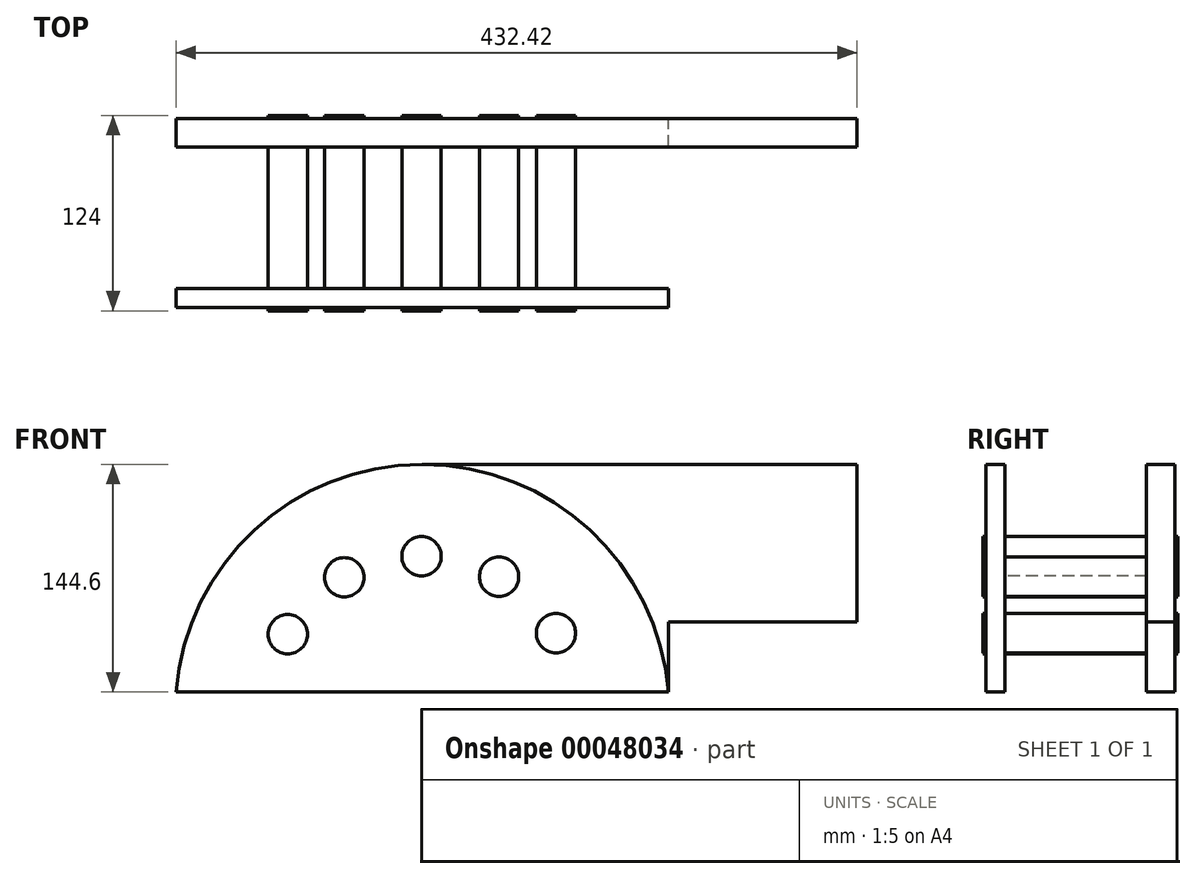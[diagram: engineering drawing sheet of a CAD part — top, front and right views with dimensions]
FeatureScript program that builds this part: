
annotation { "Feature Type Name" : "Feature", "Feature Type Description" : "" }
export const myFeature = defineFeature(function(context is Context, id is Id, definition is map)
    precondition{}
    {
        {
            var Q0;
            Q0=qCreatedBy(makeId("Front.planeOp"),FACE);
            var sketch = newSketch(context, id + "F0", { "sketchPlane" : qUnion([Q0])});
            skLineSegment(sketch, "E0.bottom", {"start": v(-26.1, 0) * mm, "end": v(-302.21, 0) * mm});
            skLineSegment(sketch, "E0.top", {"start": v(-26.1, -100) * mm, "end": v(-145.92, -100) * mm});
            skLineSegment(sketch, "E1", {"start": v(-458.51, -144.6) * mm, "end": v(-145.92, -144.6) * mm});
            skArc(sketch, "E2.trimOffspring", {"start": v(-302.21, 0) * mm, "mid": v(-408.68, -41.7) * mm, "end": v(-458.51, -144.6) * mm});
            skLineSegment(sketch, "E3", {"start": v(-145.92, -144.6) * mm, "end": v(-145.92, -100) * mm});
            skCircle(sketch, "E4", {"center": v(-302.6, -58.43) * mm, "radius": 12.5 * mm});
            skCircle(sketch, "E5.1.0", {"center": v(-351.71, -71.8) * mm, "radius": 12.5 * mm});
            skCircle(sketch, "E5.2.0", {"center": v(-387.57, -107.93) * mm, "radius": 12.5 * mm});
            skCircle(sketch, "E5.10.0", {"center": v(-217.24, -107.27) * mm, "radius": 12.5 * mm});
            skCircle(sketch, "E5.11.0", {"center": v(-253.37, -71.42) * mm, "radius": 12.5 * mm});
            skLineSegment(sketch, "E6.0", {"start": v(-26.1, 0) * mm, "end": v(-26.1, -100) * mm});
            skSolve(sketch);
        }
        {
            var Q0;
            Q0 = qSketchRegion(id + "F0", true);
            extrude(context, id + "F1", {"entities" : qUnion([Q0]), "depth" : 18 * mm});
        }
        {
            var Q0;
            Q0=makeQuery(id+"F1.opExtrude","CAP_FACE",FACE,{"disambiguationData":[OSD([sQuery(id+"F0.wireOp",EDGE,"E0.bottom"),sQuery(id+"F0.wireOp",EDGE,"E0.top"),sQuery(id+"F0.wireOp",EDGE,"E0.left"),sQuery(id+"F0.wireOp",EDGE,"E1"),sQuery(id+"F0.wireOp",EDGE,"E2.trimOffspring"),sQuery(id+"F0.wireOp",EDGE,"E3"),sQuery(id+"F0.wireOp",EDGE,"E4"),sQuery(id+"F0.wireOp",EDGE,"E5.1.0"),sQuery(id+"F0.wireOp",EDGE,"E5.2.0"),sQuery(id+"F0.wireOp",EDGE,"E5.10.0"),sQuery(id+"F0.wireOp",EDGE,"E5.11.0")])],"isStart":false});
            cPlane(context, id + "F2", {"entities" : qUnion([Q0]), "cplaneType" : CPlaneType.OFFSET, "offset" : 90 * mm, "width" : 150 * mm, "height" : 150 * mm});
        }
        {
            var Q0;
            Q0=qCreatedBy(id+"F2.planeOp",FACE);
            var sketch = newSketch(context, id + "F3", { "sketchPlane" : qUnion([Q0])});
            skArc(sketch, "E7.0", {"start": v(-145.92, -144.6) * mm, "mid": v(-302.21, 0) * mm, "end": v(-458.51, -144.6) * mm});
            skLineSegment(sketch, "E7.1", {"start": v(-458.51, -144.6) * mm, "end": v(-145.92, -144.6) * mm});
            skPoint(sketch, "E8.orphan", {"position": v(-302.21, 0) * mm});
            skCircle(sketch, "E9.0", {"center": v(-387.57, -107.93) * mm, "radius": 12.5 * mm});
            skCircle(sketch, "E9.1", {"center": v(-351.71, -71.8) * mm, "radius": 12.5 * mm});
            skCircle(sketch, "E9.2", {"center": v(-302.6, -58.43) * mm, "radius": 12.5 * mm});
            skCircle(sketch, "E9.3", {"center": v(-253.37, -71.42) * mm, "radius": 12.5 * mm});
            skCircle(sketch, "E9.4", {"center": v(-217.24, -107.27) * mm, "radius": 12.5 * mm});
            skSolve(sketch);
        }
        {
            var Q0;
            Q0=makeQuery(id+"F3.imprint","IMPRINT",FACE,{"disambiguationData":[TD([[makeQuery(id+"F3.imprint","IMPRINT",EDGE,{"derivedFrom":sQuery(id+"F3.wireOp",EDGE,"E7.0")}),1.0]])]});
            extrude(context, id + "F4", {"entities" : qUnion([Q0]), "depth" : 12 * mm});
        }
        {
            var Q0;
            Q0=makeQuery(id+"F4.opExtrude","CAP_FACE",FACE,{"disambiguationData":[OSD([sQuery(id+"F3.wireOp",EDGE,"E7.0"),sQuery(id+"F3.wireOp",EDGE,"E7.1"),sQuery(id+"F3.wireOp",EDGE,"E9.0"),sQuery(id+"F3.wireOp",EDGE,"E9.1"),sQuery(id+"F3.wireOp",EDGE,"E9.2"),sQuery(id+"F3.wireOp",EDGE,"E9.3"),sQuery(id+"F3.wireOp",EDGE,"E9.4")])],"isStart":false});
            var sketch = newSketch(context, id + "F5", { "sketchPlane" : qUnion([Q0])});
            skCircle(sketch, "E10.0", {"center": v(-387.57, -107.93) * mm, "radius": 12.5 * mm});
            skCircle(sketch, "E10.1", {"center": v(-351.71, -71.8) * mm, "radius": 12.5 * mm});
            skCircle(sketch, "E10.2", {"center": v(-302.6, -58.43) * mm, "radius": 12.5 * mm});
            skCircle(sketch, "E10.3", {"center": v(-253.37, -71.42) * mm, "radius": 12.5 * mm});
            skCircle(sketch, "E10.4", {"center": v(-217.24, -107.27) * mm, "radius": 12.5 * mm});
            skSolve(sketch);
        }
        {
            var Q0;
            Q0=makeQuery(id+"F5.imprint","IMPRINT",FACE,{"disambiguationData":[TD([[makeQuery(id+"F5.imprint","IMPRINT",EDGE,{"derivedFrom":sQuery(id+"F5.wireOp",EDGE,"E10.0")}),1.0]])]});
            var Q1;
            Q1=makeQuery(id+"F5.imprint","IMPRINT",FACE,{"disambiguationData":[TD([[makeQuery(id+"F5.imprint","IMPRINT",EDGE,{"derivedFrom":sQuery(id+"F5.wireOp",EDGE,"E10.1")}),1.0]])]});
            var Q2;
            Q2=makeQuery(id+"F5.imprint","IMPRINT",FACE,{"disambiguationData":[TD([[makeQuery(id+"F5.imprint","IMPRINT",EDGE,{"derivedFrom":sQuery(id+"F5.wireOp",EDGE,"E10.2")}),1.0]])]});
            var Q3;
            Q3=makeQuery(id+"F5.imprint","IMPRINT",FACE,{"disambiguationData":[TD([[makeQuery(id+"F5.imprint","IMPRINT",EDGE,{"derivedFrom":sQuery(id+"F5.wireOp",EDGE,"E10.3")}),1.0]])]});
            var Q4;
            Q4=makeQuery(id+"F5.imprint","IMPRINT",FACE,{"disambiguationData":[TD([[makeQuery(id+"F5.imprint","IMPRINT",EDGE,{"derivedFrom":sQuery(id+"F5.wireOp",EDGE,"E10.4")}),1.0]])]});
            var Q5;
            Q5=makeQuery(id+"F1.opExtrude","CAP_FACE",FACE,{"disambiguationData":[OSD([sQuery(id+"F0.wireOp",EDGE,"E0.bottom"),sQuery(id+"F0.wireOp",EDGE,"E0.top"),sQuery(id+"F0.wireOp",EDGE,"E0.left"),sQuery(id+"F0.wireOp",EDGE,"E1"),sQuery(id+"F0.wireOp",EDGE,"E2.trimOffspring"),sQuery(id+"F0.wireOp",EDGE,"E3"),sQuery(id+"F0.wireOp",EDGE,"E4"),sQuery(id+"F0.wireOp",EDGE,"E5.1.0"),sQuery(id+"F0.wireOp",EDGE,"E5.2.0"),sQuery(id+"F0.wireOp",EDGE,"E5.10.0"),sQuery(id+"F0.wireOp",EDGE,"E5.11.0")])],"isStart":true});
            extrude(context, id + "F6", {"entities" : qUnion([Q0, Q1, Q2, Q3, Q4]), "operationType" : NewBodyOperationType.ADD, "oppositeDirection" : true, "endBoundEntityFace" : qUnion([Q5]), "depth" : 122 * mm, "hasSecondDirection" : true, "secondDirectionOppositeDirection" : false, "secondDirectionDepth" : 2 * mm});
        }
    });
